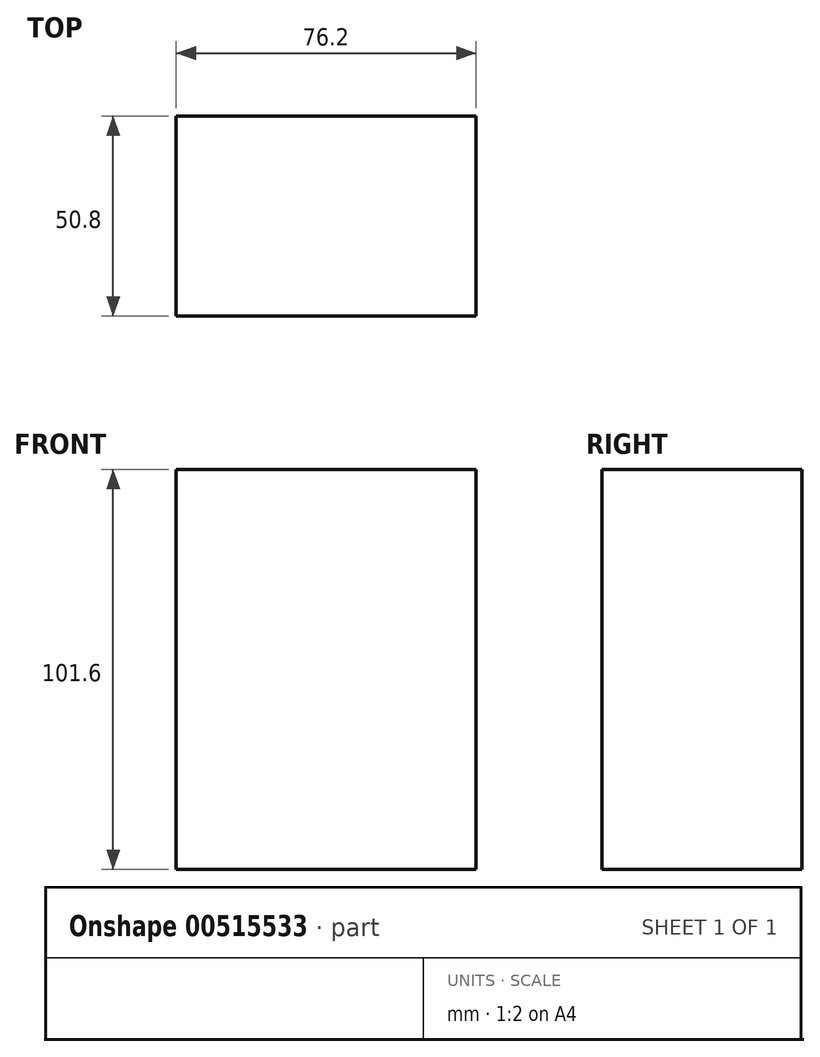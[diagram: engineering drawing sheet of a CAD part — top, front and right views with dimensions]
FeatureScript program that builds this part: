
annotation { "Feature Type Name" : "Feature", "Feature Type Description" : "" }
export const myFeature = defineFeature(function(context is Context, id is Id, definition is map)
    precondition{}
    {
        {
            var Q0;
            Q0=qCreatedBy(makeId("Right.planeOp"),FACE);
            var sketch = newSketch(context, id + "F0", { "sketchPlane" : qUnion([Q0])});
            skLineSegment(sketch, "E0", {"start": v(25.4, 101.6) * mm, "end": v(-25.4, 101.6) * mm});
            skLineSegment(sketch, "E1", {"start": v(-25.4, 101.6) * mm, "end": v(-25.4, 0) * mm});
            skLineSegment(sketch, "E2", {"start": v(-25.4, 0) * mm, "end": v(25.4, 0) * mm});
            skLineSegment(sketch, "E3", {"start": v(25.4, 101.6) * mm, "end": v(25.4, 0) * mm});
            skSolve(sketch);
        }
        {
            var Q0;
            Q0=makeQuery(id+"F0.imprint","IMPRINT",FACE,{"disambiguationData":[TD([[makeQuery(id+"F0.imprint","IMPRINT",EDGE,{"derivedFrom":sQuery(id+"F0.wireOp",EDGE,"E0")}),1.0]])]});
            extrude(context, id + "F1", {"entities" : qUnion([Q0]), "depth" : 76.2 * mm, "offsetDistance" : 25.4 * mm});
        }
    });
